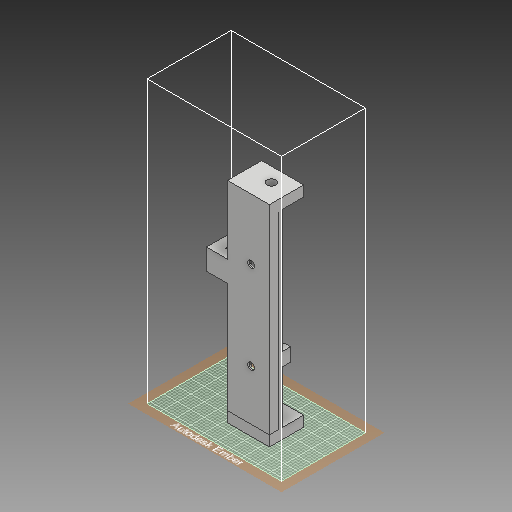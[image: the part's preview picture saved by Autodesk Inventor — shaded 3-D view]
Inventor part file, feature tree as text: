
AUTODESK INVENTOR PART (.ipt)
format: ipt  version: 2018 (Build 220112000, 112)  size: 775,680 bytes
history: native  units: mm
features: sketch x66, extrude x49, hole x8, fillet x6
ambient origin geometry x8: Origin, YZ Plane, XZ Plane, XY Plane, X Axis, Y Axis, Z Axis, Center Point
bodies: Solid1 (feature_tree)
feature tree (129):
  extrude  "Extrusion1"  Depth=100.0mm
  extrude  "Extrusion2"  Depth=5.0mm
  sketch  "Sketch3"  dims[d5=5.0mm d6=40.0mm d7=0.0mm]
  hole  "Hole1"  [1 undecoded]
  extrude  "Extrusion3"  Depth=2.0mm
  hole  "Hole2"  [1 undecoded]
  fillet  "Fillet1"  Radius=8.5mm
  extrude  "Extrusion4"  TaperAngle=90.0deg  [1 undecoded]
  extrude  "Extrusion5"  TaperAngle=180.0deg  [1 undecoded]
  hole  "Hole3"  [1 undecoded]
  fillet  "Fillet2"  Radius=3.5mm
  extrude  "Extrusion6"  Depth=10.0mm
  extrude  "Extrusion7"  Depth=5.0mm TaperAngle=0.0deg
  extrude  "Extrusion8"  Depth=5.0mm TaperAngle=0.0deg
  extrude  "Extrusion9"  Depth=0.1mm
  hole  "Hole4"  [1 undecoded]
  extrude  "Extrusion10"  Depth=5.5mm
  hole  "Hole5"  [1 undecoded]
  extrude  "Extrusion11"  Depth=2.1mm TaperAngle=0.0deg
  extrude  "Extrusion12"  Depth=5.0mm
  extrude  "Extrusion13"  Depth=1.0mm TaperAngle=0.0deg
  extrude  "Extrusion14"  Depth=3.8mm TaperAngle=0.0deg
  sketch  "Sketch21"  dims[d66=6.35mm d67=3.8mm d68=0.0mm]
  extrude  "Extrusion15"  Depth=8.0mm TaperAngle=0.0deg
  sketch  "Sketch23"  dims[d78=3.3mm d79=6.0mm d80=4.0mm d81=2.0mm d82=90.0deg d83=80.0mm d84=20.594885mm d85=5.45mm]
  extrude  "Extrusion16"  Depth=2.0mm
  extrude  "Extrusion17"  Depth=10.5mm
  hole  "Hole6"  [1 undecoded]
  fillet  "Fillet3"  Radius=4.5mm
  extrude  "Extrusion18"  Depth=8.0mm TaperAngle=0.0deg
  sketch  "Sketch28"  dims[d100=4.1mm d101=0.0mm d102=5.0mm]
  extrude  "Extrusion19"  Depth=10.0mm
  extrude  "Extrusion20"  Depth=5.0mm
  extrude  "Extrusion21"  Depth=10.0mm TaperAngle=0.0deg
  hole  "Hole7"  [1 undecoded]
  extrude  "Extrusion22"  Depth=21.0mm
  extrude  "Extrusion23"  Depth=118.0mm TaperAngle=0.0deg
  fillet  "Fillet4"  Radius=50.0mm
  fillet  "Fillet5"  Radius=7.499983mm
  extrude  "Extrusion24"  Depth=10.0mm
  extrude  "Extrusion25"  Depth=4.1mm TaperAngle=0.0deg
  hole  "Hole8"  [1 undecoded]
  extrude  "Extrusion26"  Depth=8.0mm TaperAngle=0.0deg
  sketch  "Sketch39"  dims[d142=3.85mm d143=0.0mm d144=3.0mm]
  extrude  "Extrusion27"  Depth=1.0mm
  extrude  "Extrusion28"  Depth=3.0mm
  extrude  "Extrusion29"  Depth=100.0mm TaperAngle=0.0deg
  extrude  "Extrusion30"  Depth=10.0mm
  extrude  "Extrusion31"  Depth=5.0mm
  fillet  "Fillet6"  Radius=7.5mm
  extrude  "Extrusion32"  Depth=8.0mm
  sketch  "Sketch46"  dims[d167=2.0mm d168=0.0mm d169=2.0mm d170=0.0mm]
  extrude  "Extrusion33"  Depth=5.0mm TaperAngle=0.0deg
  sketch  "Sketch48"  dims[d174=3.3mm d175=10.0mm d176=0.0mm]
  extrude  "Extrusion34"  Depth=2.0mm TaperAngle=0.0deg
  extrude  "Extrusion35"  Depth=2.0mm
  sketch  "Sketch51"  dims[d182=5.0mm d183=9.5mm d184=0.0mm]
  extrude  "Extrusion36"  Depth=10.0mm TaperAngle=0.0deg
  sketch  "Sketch53"  dims[d189=5.0mm d190=3.5mm]
  extrude  "Extrusion37"  Depth=2.0mm
  sketch  "Sketch55"  dims[d194=8.5mm d195=12.0mm]
  extrude  "Extrusion38"  Depth=5.0mm
  extrude  "Extrusion39"  Depth=9.5mm TaperAngle=0.0deg
  extrude  "Extrusion40"  Depth=9.5mm TaperAngle=0.0deg
  extrude  "Extrusion41"  Depth=5.0mm
  extrude  "Extrusion42"  Depth=9.5mm TaperAngle=0.0deg
  extrude  "Extrusion43"  Depth=12.0mm
  extrude  "Extrusion44"  Depth=12.0mm
  extrude  "Extrusion45"  Depth=3.5mm TaperAngle=0.0deg
  extrude  "Extrusion46"  Depth=3.5mm TaperAngle=0.0deg
  extrude  "Extrusion47"  Depth=3.2mm TaperAngle=0.0deg
  extrude  "Extrusion48"  Depth=3.2mm TaperAngle=0.0deg
  extrude  "Extrusion49"  Depth=101.0mm TaperAngle=0.0deg
  sketch  "Sketch1"  dims[d0=22.65mm d1=100.0mm]
  sketch  "Sketch2"  dims[d2=5.0mm d3=0.0mm d4=5.0mm]
  sketch  "Sketch4"  dims[d8=10.0mm]
  sketch  "Sketch5"  dims[d9=4.0mm d10=6.0mm d11=4.0mm d12=2.0mm d13=90.0deg d14=115.0mm d15=20.594885mm d16=23.0mm]
  sketch  "Sketch6"  dims[d17=102.75mm d18=0.0mm d19=1.175mm d20=8.5mm]
  sketch  "Sketch7"  dims[d21=21.0mm d22=90.0deg]
  sketch  "Sketch8"  dims[d23=8.5mm d24=180.0deg]
  sketch  "Sketch9"  dims[d25=21.0mm]
  sketch  "Sketch10"  dims[d26=4.0mm d27=6.0mm d28=4.0mm d29=2.0mm d30=90.0deg d31=115.0mm d32=20.594885mm d33=1.0mm d34=3.5mm]
  sketch  "Sketch11"  dims[d35=15.825mm d36=10.0mm]
  sketch  "Sketch12"  dims[d37=10.0mm d38=5.0mm d39=0.0mm]
  sketch  "Sketch13"  dims[d40=5.0mm d41=12.5mm d42=0.0mm]
  sketch  "Sketch14"  dims[d43=6.0mm d44=6.0mm d45=4.0mm d46=2.0mm d47=90.0deg d48=115.0mm d49=20.594885mm d50=0.1mm]
  sketch  "Sketch15"  dims[d51=4.25mm d52=1000.0mm d53=0.0mm]
  sketch  "Sketch16"  dims[d54=3.3mm d55=5.5mm]
  sketch  "Sketch17"  dims[d56=3.2mm d57=3.0mm]
  sketch  "Sketch18"  dims[d58=2.1mm d59=91.25mm d60=0.0mm]
  sketch  "Sketch19"  dims[d61=4.44mm d62=5.0mm]
  sketch  "Sketch20"  dims[d63=1.0mm d64=91.25mm d65=0.0mm]
  sketch  "Sketch22"  dims[d69=3.3mm d70=6.0mm d71=4.0mm d72=2.0mm d73=90.0deg d74=8.0mm d75=20.594885mm d76=4.55mm d77=0.0mm]
  sketch  "Sketch24"  dims[d86=129.8mm d87=0.0mm d88=10.5mm]
  sketch  "Sketch25"  dims[d89=2.5mm d90=0.0mm d91=10.0mm d92=4.5mm d93=0.0mm]
  sketch  "Sketch26"  dims[d94=8.0mm d95=0.0mm d96=15.5mm d97=0.0mm]
  sketch  "Sketch27"  dims[d98=10.0mm d99=10.0mm]
  sketch  "Sketch29"  dims[d103=17.5mm d104=10.0mm d105=0.0mm]
  sketch  "Sketch30"  dims[d106=5.0mm]
  sketch  "Sketch31"  dims[d107=6.0mm d108=6.0mm d109=4.0mm d110=2.0mm d111=90.0deg d112=80.0mm d113=20.594885mm d114=2.0mm]
  sketch  "Sketch32"  dims[d115=45.0mm d116=0.0mm d117=21.0mm]
  sketch  "Sketch33"  dims[d118=4.5mm d119=118.0mm d120=0.0mm d121=50.0mm d122=7.499983mm]
  sketch  "Sketch34"  dims[d123=7.5mm d124=10.0mm]
  sketch  "Sketch35"  dims[d125=10.0mm d126=4.1mm d127=0.0mm]
  sketch  "Sketch36"  dims[d128=13.4mm d129=0.0mm d130=5.0mm]
  sketch  "Sketch37"  dims[d131=6.0mm d132=6.0mm d133=4.0mm d134=2.0mm d135=90.0deg d136=8.0mm d137=20.594885mm d138=130.4mm d139=0.0mm]
  sketch  "Sketch38"  dims[d140=1.0mm d141=1.0mm]
  sketch  "Sketch40"  dims[d145=2.0mm d146=100.0mm d147=0.0mm]
  sketch  "Sketch41"  dims[d148=4.0mm d149=10.0mm]
  sketch  "Sketch42"  dims[d150=5.0mm d151=15.0mm d152=7.5mm]
  sketch  "Sketch43"  dims[d153=7.5mm d154=0.0mm]
  sketch  "Sketch44"  dims[d155=6.0mm d156=6.0mm d157=4.0mm d158=2.0mm d159=90.0deg d160=8.0mm d161=20.594885mm d162=5.5mm]
  sketch  "Sketch45"  dims[d163=5.0mm d164=0.0mm d165=5.5mm d166=0.0mm]
  sketch  "Sketch47"  dims[d171=2.0mm d172=0.0mm d173=20.0mm]
  sketch  "Sketch49"  dims[d177=2.0mm d178=3.5mm]
  sketch  "Sketch50"  dims[d179=5.0mm d180=0.0mm d181=8.5mm]
  sketch  "Sketch52"  dims[d185=9.5mm d186=0.0mm d187=2.7mm d188=0.0mm]
  sketch  "Sketch54"  dims[d191=7.5mm d192=9.5mm d193=0.0mm]
  sketch  "Sketch56"  dims[d196=10.25mm d197=0.0mm d198=12.0mm]
  sketch  "Sketch57"  dims[d199=10.25mm d200=0.0mm d201=3.5mm d202=0.0mm]
  sketch  "Sketch58"  dims[d203=3.75mm d204=3.5mm d205=0.0mm]
  sketch  "Sketch59"  dims[d206=9.6mm d207=3.2mm d208=0.0mm]
  sketch  "Sketch60"  dims[d209=9.6mm d210=3.2mm d211=0.0mm]
  sketch  "Sketch61"  dims[d212=5.5mm d213=101.0mm d214=0.0mm]
  sketch  "Sketch62"  dims[d215=3.5mm d216=0.0mm]
  sketch  "Sketch63"  dims[d217=4.0mm]
  sketch  "Sketch64"  dims[d218=4.0mm d219=0.0mm]
  sketch  "Sketch65"  dims[d220=9.7mm]
  sketch  "Sketch66"  dims[d221=106.25mm d222=0.0mm d223=9.8mm d224=1.8mm d225=0.0mm d226=9.8mm d227=1.8mm d228=0.0mm d229=5.0mm d230=180.0mm d231=0.0mm]
note: 10 required parameter values undecoded (feature->parameter linkage not recoverable at this tier; creation-order binding heuristic only, values carry confidence <= 0.55)
